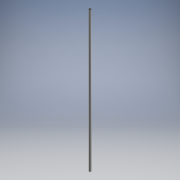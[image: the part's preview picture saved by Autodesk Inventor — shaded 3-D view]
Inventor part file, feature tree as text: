
AUTODESK INVENTOR PART (.ipt)
format: ipt  version: 2018.3 (Build 223284000, 284)  size: 93,696 bytes
history: native  units: mm
features: other x1, extrude x1, sketch x1
ambient origin geometry x8: Origin, YZ Plane, XZ Plane, XY Plane, X Axis, Y Axis, Z Axis, Center Point
bodies: Body1 (feature_tree)
feature tree (3):
  other  "ソリッド1"
  extrude  "押し出し1"  Depth=1.5mm
  sketch  "スケッチ1"
